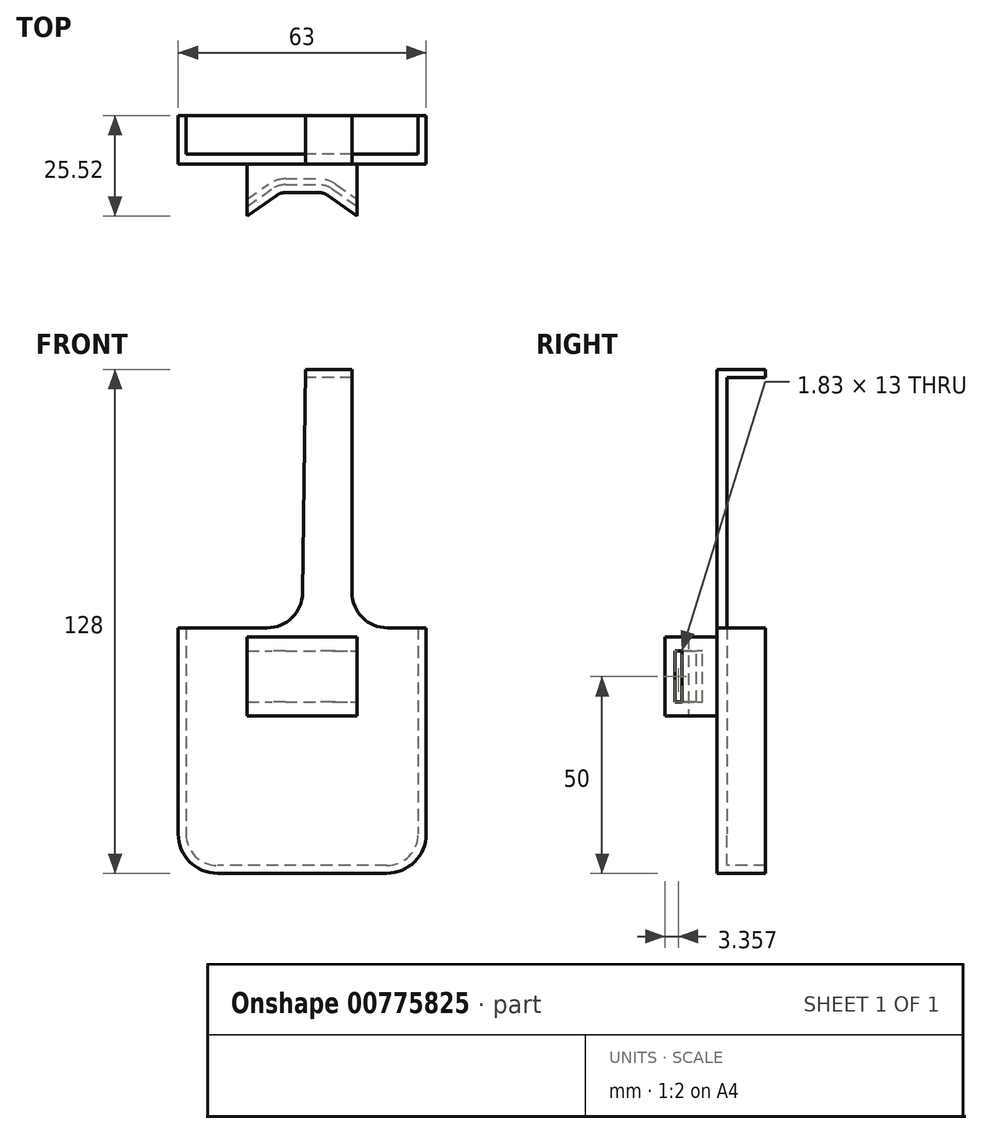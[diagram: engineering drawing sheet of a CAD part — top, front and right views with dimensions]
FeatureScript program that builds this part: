
annotation { "Feature Type Name" : "Feature", "Feature Type Description" : "" }
export const myFeature = defineFeature(function(context is Context, id is Id, definition is map)
    precondition{}
    {
        {
            var Q0;
            Q0=qCreatedBy(makeId("Top.planeOp"),FACE);
            cPlane(context, id + "F0", {"entities" : qUnion([Q0]), "cplaneType" : CPlaneType.OFFSET, "offset" : 10 * mm, "width" : 150 * mm, "height" : 150 * mm});
        }
        {
            var Q0;
            Q0=qCreatedBy(makeId("Top.planeOp"),FACE);
            var sketch = newSketch(context, id + "F1", { "sketchPlane" : qUnion([Q0])});
            skLineSegment(sketch, "E0.bottom", {"start": v(-14, 5.51) * mm, "end": v(14, 5.51) * mm});
            skLineSegment(sketch, "E0.left", {"start": v(-14, 5.51) * mm, "end": v(-14, -7.7) * mm});
            skLineSegment(sketch, "E0.right", {"start": v(14, 5.51) * mm, "end": v(14, -7.7) * mm});
            skLineSegment(sketch, "E1", {"start": v(-14, -7.7) * mm, "end": v(-6.53, -2.48) * mm});
            skLineSegment(sketch, "E2", {"start": v(-4.24, -1.76) * mm, "end": v(4.24, -1.76) * mm});
            skLineSegment(sketch, "E3", {"start": v(6.53, -2.48) * mm, "end": v(14, -7.7) * mm});
            skPoint(sketch, "E4.visualSharp", {"position": v(-5.5, -1.76) * mm});
            skArc(sketch, "E4.filletArc", {"start": v(-4.24, -1.76) * mm, "mid": v(-5.44, -1.94) * mm, "end": v(-6.53, -2.48) * mm});
            skPoint(sketch, "E5.visualSharp", {"position": v(5.5, -1.76) * mm});
            skArc(sketch, "E5.filletArc", {"start": v(6.53, -2.48) * mm, "mid": v(5.44, -1.94) * mm, "end": v(4.24, -1.76) * mm});
            skSolve(sketch);
        }
        {
            var Q0;
            Q0=makeQuery(id+"F1.imprint","IMPRINT",FACE,{"disambiguationData":[TD([[makeQuery(id+"F1.imprint","IMPRINT",EDGE,{"derivedFrom":sQuery(id+"F1.wireOp",EDGE,"E0.bottom")}),-1.0]])]});
            extrude(context, id + "F2", {"entities" : qUnion([Q0]), "depth" : 20 * mm, "offsetDistance" : 25 * mm});
        }
        {
            var Q0;
            Q0=qCreatedBy(id+"F0.planeOp",FACE);
            var sketch = newSketch(context, id + "F3", { "sketchPlane" : qUnion([Q0])});
            skLineSegment(sketch, "E6.0", {"start": v(7.68, -0.84) * mm, "end": v(15.15, -6.07) * mm});
            skLineSegment(sketch, "E6.1", {"start": v(-15.15, -6.07) * mm, "end": v(-7.68, -0.84) * mm});
            skArc(sketch, "E6.2", {"start": v(-4.24, 0.24) * mm, "mid": v(-6.04, -0.04) * mm, "end": v(-7.68, -0.84) * mm});
            skLineSegment(sketch, "E6.3", {"start": v(-4.24, 0.24) * mm, "end": v(4.24, 0.24) * mm});
            skArc(sketch, "E6.4", {"start": v(7.68, -0.84) * mm, "mid": v(6.04, -0.04) * mm, "end": v(4.24, 0.24) * mm});
            skLineSegment(sketch, "E7.0", {"start": v(8.54, 0.39) * mm, "end": v(16, -4.84) * mm});
            skLineSegment(sketch, "E7.1", {"start": v(-16, -4.84) * mm, "end": v(-8.54, 0.39) * mm});
            skArc(sketch, "E7.2", {"start": v(-4.24, 1.74) * mm, "mid": v(-6.5, 1.4) * mm, "end": v(-8.54, 0.39) * mm});
            skLineSegment(sketch, "E7.3", {"start": v(-4.24, 1.74) * mm, "end": v(4.24, 1.74) * mm});
            skArc(sketch, "E7.4", {"start": v(8.54, 0.39) * mm, "mid": v(6.5, 1.4) * mm, "end": v(4.24, 1.74) * mm});
            skLineSegment(sketch, "E8", {"start": v(16, -4.84) * mm, "end": v(15.15, -6.07) * mm});
            skLineSegment(sketch, "E9", {"start": v(-16, -4.84) * mm, "end": v(-15.15, -6.07) * mm});
            skSolve(sketch);
        }
        {
            var Q0;
            Q0=makeQuery(id+"F3.imprint","IMPRINT",FACE,{"disambiguationData":[TD([[makeQuery(id+"F3.imprint","IMPRINT",EDGE,{"derivedFrom":sQuery(id+"F3.wireOp",EDGE,"E6.0")}),1.0]])]});
            extrude(context, id + "F4", {"entities" : qUnion([Q0]), "operationType" : NewBodyOperationType.REMOVE, "endBound" : BoundingType.SYMMETRIC, "oppositeDirection" : true, "depth" : 13 * mm, "offsetDistance" : 25 * mm});
        }
        {
            var Q0;
            Q0=makeQuery(id+"F2.opExtrude","SWEPT_FACE",FACE,{"disambiguationData":[OSD([sQuery(id+"F1.wireOp",EDGE,"E0.bottom")])]});
            var sketch = newSketch(context, id + "F5", { "sketchPlane" : qUnion([Q0])});
            skLineSegment(sketch, "E10.bottom", {"start": v(-21.5, 88) * mm, "end": v(21.5, 88) * mm});
            skLineSegment(sketch, "E10.top", {"start": v(-21.5, -40) * mm, "end": v(21.5, -40) * mm});
            skLineSegment(sketch, "E10.left", {"start": v(-31.5, 78) * mm, "end": v(-31.5, -30) * mm});
            skLineSegment(sketch, "E10.right", {"start": v(31.5, 78) * mm, "end": v(31.5, -30) * mm});
            skPoint(sketch, "E11.visualSharp", {"position": v(-31.5, -40) * mm});
            skArc(sketch, "E11.filletArc", {"start": v(-31.5, -30) * mm, "mid": v(-28.57, -37.07) * mm, "end": v(-21.5, -40) * mm});
            skPoint(sketch, "E12.visualSharp", {"position": v(31.5, -40) * mm});
            skArc(sketch, "E12.filletArc", {"start": v(21.5, -40) * mm, "mid": v(28.57, -37.07) * mm, "end": v(31.5, -30) * mm});
            skPoint(sketch, "E13.visualSharp", {"position": v(-31.5, 88) * mm});
            skArc(sketch, "E13.filletArc", {"start": v(-21.5, 88) * mm, "mid": v(-28.57, 85.07) * mm, "end": v(-31.5, 78) * mm});
            skPoint(sketch, "E14.visualSharp", {"position": v(31.5, 88) * mm});
            skArc(sketch, "E14.filletArc", {"start": v(31.5, 78) * mm, "mid": v(28.57, 85.07) * mm, "end": v(21.5, 88) * mm});
            skSolve(sketch);
        }
        {
            var Q0;
            Q0=qCreatedBy(makeId("Front.planeOp"),FACE);
            var sketch = newSketch(context, id + "F6", { "sketchPlane" : qUnion([Q0])});
            skLineSegment(sketch, "E15", {"start": v(21.68, 22.36) * mm, "end": v(32.07, 22.36) * mm});
            skLineSegment(sketch, "E16", {"start": v(32.07, 22.36) * mm, "end": v(32.07, 102.72) * mm});
            skLineSegment(sketch, "E17", {"start": v(32.07, 102.72) * mm, "end": v(12.68, 102.83) * mm});
            skPoint(sketch, "E18.visualSharp", {"position": v(14.84, 22.36) * mm});
            skArc(sketch, "E18.filletArc", {"start": v(12.68, 31.36) * mm, "mid": v(15.32, 25) * mm, "end": v(21.68, 22.36) * mm});
            skLineSegment(sketch, "E19", {"start": v(12.68, 102.83) * mm, "end": v(12.68, 31.36) * mm});
            skLineSegment(sketch, "E20.MirrorCS", {"start": v(1.12, 102.83) * mm, "end": v(0.12, 31.23) * mm});
            skLineSegment(sketch, "E21", {"start": v(-38.7, 22.36) * mm, "end": v(-8.88, 22.36) * mm});
            skPoint(sketch, "E22.visualSharp", {"position": v(0, 22.36) * mm});
            skArc(sketch, "E22.filletArc", {"start": v(-8.88, 22.36) * mm, "mid": v(-2.56, 24.95) * mm, "end": v(0.12, 31.23) * mm});
            skLineSegment(sketch, "E23", {"start": v(1.12, 102.83) * mm, "end": v(-38.7, 102.83) * mm});
            skLineSegment(sketch, "E24", {"start": v(-38.7, 102.83) * mm, "end": v(-38.7, 22.36) * mm});
            skSolve(sketch);
        }
        {
            var Q0;
            Q0 = qSketchRegion(id + "F5", true);
            extrude(context, id + "F7", {"entities" : qUnion([Q0]), "depth" : 2.5 * mm, "offsetDistance" : 25 * mm});
        }
        {
            var Q0;
            Q0=makeQuery(id+"F7.opExtrude","CAP_FACE",FACE,{"disambiguationData":[OSD([sQuery(id+"F5.wireOp",EDGE,"E10.bottom"),sQuery(id+"F5.wireOp",EDGE,"E10.top"),sQuery(id+"F5.wireOp",EDGE,"E10.left"),sQuery(id+"F5.wireOp",EDGE,"E10.right"),sQuery(id+"F5.wireOp",EDGE,"E11.filletArc"),sQuery(id+"F5.wireOp",EDGE,"E12.filletArc"),sQuery(id+"F5.wireOp",EDGE,"E13.filletArc"),sQuery(id+"F5.wireOp",EDGE,"E14.filletArc")])],"isStart":false});
            var sketch = newSketch(context, id + "F8", { "sketchPlane" : qUnion([Q0])});
            skArc(sketch, "E25.0", {"start": v(-31.5, -30) * mm, "mid": v(-28.57, -37.07) * mm, "end": v(-21.5, -40) * mm});
            skLineSegment(sketch, "E26.0", {"start": v(-31.5, 78) * mm, "end": v(-31.5, -30) * mm});
            skLineSegment(sketch, "E27.0", {"start": v(-21.5, -40) * mm, "end": v(21.5, -40) * mm});
            skLineSegment(sketch, "E27.1", {"start": v(31.5, 78) * mm, "end": v(31.5, -30) * mm});
            skArc(sketch, "E27.2", {"start": v(21.5, -40) * mm, "mid": v(28.57, -37.07) * mm, "end": v(31.5, -30) * mm});
            skArc(sketch, "E27.3", {"start": v(-21.5, 88) * mm, "mid": v(-28.57, 85.07) * mm, "end": v(-31.5, 78) * mm});
            skLineSegment(sketch, "E27.4", {"start": v(-21.5, 88) * mm, "end": v(21.5, 88) * mm});
            skArc(sketch, "E27.5", {"start": v(31.5, 78) * mm, "mid": v(28.57, 85.07) * mm, "end": v(21.5, 88) * mm});
            skLineSegment(sketch, "E28.0", {"start": v(-29.5, 78) * mm, "end": v(-29.5, -30) * mm});
            skArc(sketch, "E28.1", {"start": v(-21.5, 86) * mm, "mid": v(-27.16, 83.66) * mm, "end": v(-29.5, 78) * mm});
            skArc(sketch, "E28.2", {"start": v(-29.5, -30) * mm, "mid": v(-27.16, -35.66) * mm, "end": v(-21.5, -38) * mm});
            skLineSegment(sketch, "E28.3", {"start": v(-21.5, 86) * mm, "end": v(21.5, 86) * mm});
            skLineSegment(sketch, "E28.4", {"start": v(-21.5, -38) * mm, "end": v(21.5, -38) * mm});
            skArc(sketch, "E28.5", {"start": v(21.5, -38) * mm, "mid": v(27.16, -35.66) * mm, "end": v(29.5, -30) * mm});
            skLineSegment(sketch, "E28.6", {"start": v(29.5, 78) * mm, "end": v(29.5, -30) * mm});
            skArc(sketch, "E28.7", {"start": v(29.5, 78) * mm, "mid": v(27.16, 83.66) * mm, "end": v(21.5, 86) * mm});
            skSolve(sketch);
        }
        {
            var Q0;
            Q0 = qSketchRegion(id + "F8", true);
            extrude(context, id + "F9", {"entities" : qUnion([Q0]), "operationType" : NewBodyOperationType.ADD, "depth" : 9.8 * mm, "offsetDistance" : 25 * mm});
        }
        {
            var Q0;
            Q0 = qSketchRegion(id + "F6", true);
            extrude(context, id + "F10", {"entities" : qUnion([Q0]), "operationType" : NewBodyOperationType.REMOVE, "oppositeDirection" : true, "depth" : 25 * mm, "offsetDistance" : 25 * mm});
        }
    });
